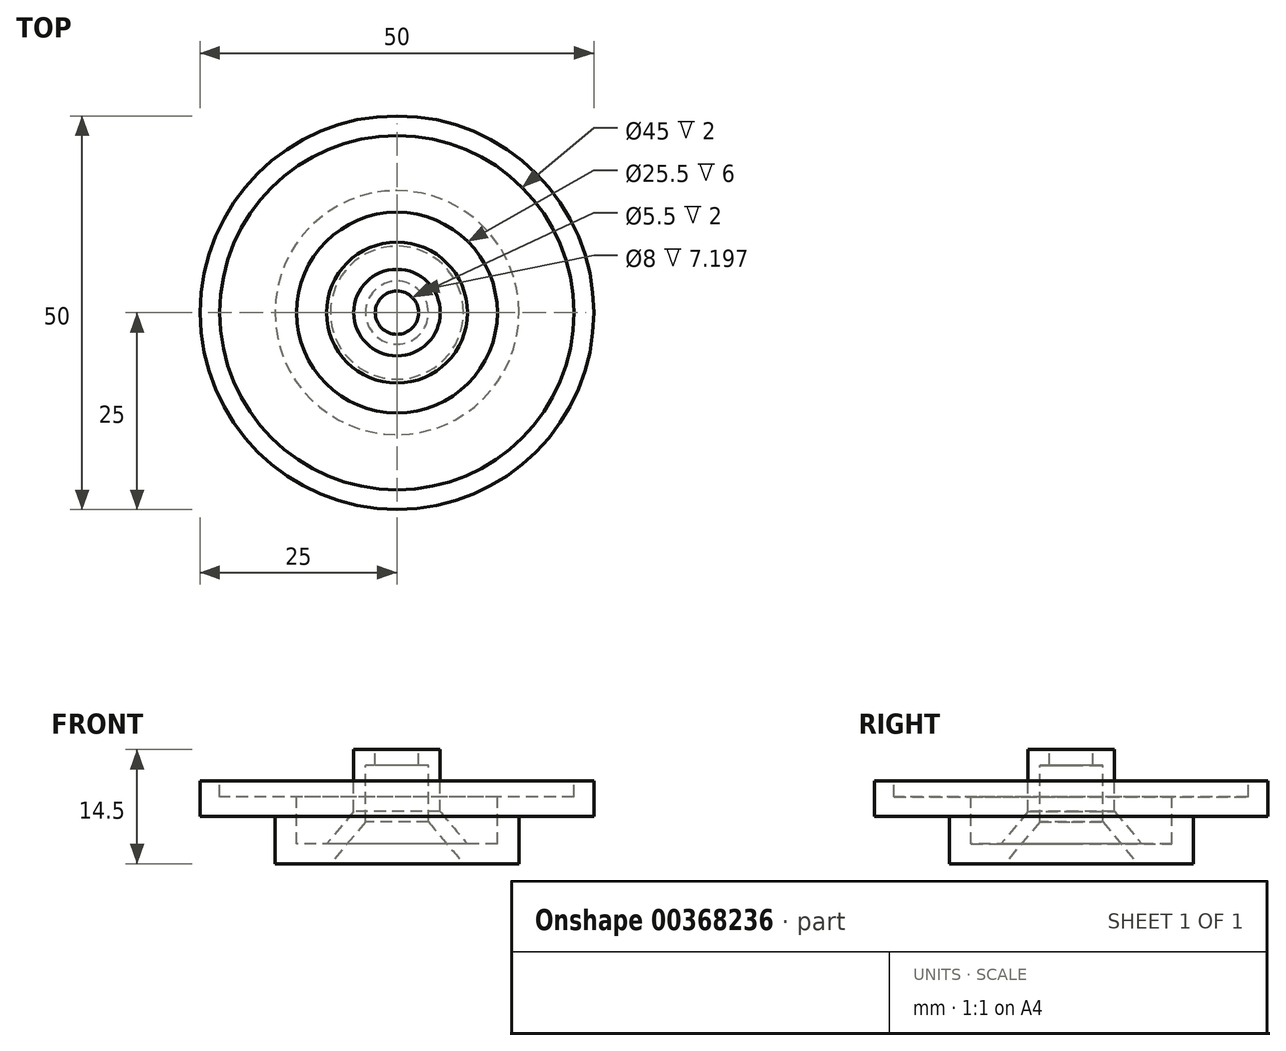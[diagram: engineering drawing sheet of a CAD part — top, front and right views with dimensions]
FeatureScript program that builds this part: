
annotation { "Feature Type Name" : "Feature", "Feature Type Description" : "" }
export const myFeature = defineFeature(function(context is Context, id is Id, definition is map)
    precondition{}
    {
        {
            var Q0;
            Q0=qCreatedBy(makeId("Front.planeOp"),FACE);
            var sketch = newSketch(context, id + "F0", { "sketchPlane" : qUnion([Q0])});
            skLineSegment(sketch, "E0", {"start": v(15.5, 0) * mm, "end": v(15.5, 6) * mm});
            skLineSegment(sketch, "E1", {"start": v(15.5, 6) * mm, "end": v(25, 6) * mm});
            skLineSegment(sketch, "E2", {"start": v(25, 6) * mm, "end": v(25, 10.5) * mm});
            skLineSegment(sketch, "E3", {"start": v(25, 10.5) * mm, "end": v(22.5, 10.5) * mm});
            skLineSegment(sketch, "E4", {"start": v(22.5, 10.5) * mm, "end": v(22.5, 8.5) * mm});
            skLineSegment(sketch, "E5", {"start": v(22.5, 8.5) * mm, "end": v(12.75, 8.5) * mm});
            skLineSegment(sketch, "E6", {"start": v(5.5, 8.5) * mm, "end": v(5.5, 10.5) * mm});
            skLineSegment(sketch, "E7", {"start": v(12.75, 8.5) * mm, "end": v(12.75, 2.5) * mm});
            skLineSegment(sketch, "E8", {"start": v(0, 20.78) * mm, "end": v(0, -15.3) * mm, "construction": true});
            skLineSegment(sketch, "E9", {"start": v(12.75, 2.5) * mm, "end": v(8.95, 2.5) * mm});
            skLineSegment(sketch, "E10", {"start": v(8.95, 2.5) * mm, "end": v(5.5, 6.61) * mm});
            skLineSegment(sketch, "E11", {"start": v(5.5, 8.5) * mm, "end": v(5.5, 6.61) * mm});
            skLineSegment(sketch, "E12", {"start": v(5.5, 10.5) * mm, "end": v(5.5, 14.5) * mm});
            skLineSegment(sketch, "E13", {"start": v(15.5, 0) * mm, "end": v(8.45, 0) * mm});
            skLineSegment(sketch, "E14.trimOffspring", {"start": v(8.45, 0) * mm, "end": v(15.5, 0) * mm});
            skLineSegment(sketch, "E15", {"start": v(4, 12.5) * mm, "end": v(4, 5.3) * mm});
            skLineSegment(sketch, "E16", {"start": v(8.45, 0) * mm, "end": v(4, 5.3) * mm});
            skPoint(sketch, "E17.end.orphan", {"position": v(0, 14.5) * mm});
            skPoint(sketch, "E18.start.orphan", {"position": v(0, 12.5) * mm});
            skLineSegment(sketch, "E19", {"start": v(5.5, 14.5) * mm, "end": v(2.75, 14.5) * mm});
            skLineSegment(sketch, "E20", {"start": v(2.75, 14.5) * mm, "end": v(2.75, 12.5) * mm});
            skLineSegment(sketch, "E21", {"start": v(2.75, 12.5) * mm, "end": v(4, 12.5) * mm});
            skSolve(sketch);
        }
        {
            var Q0;
            Q0=makeQuery(id+"F0.imprint","IMPRINT",FACE,{"disambiguationData":[TD([[makeQuery(id+"F0.imprint","IMPRINT",EDGE,{"derivedFrom":sQuery(id+"F0.wireOp",EDGE,"E0")}),1.0]])]});
            var Q1;
            Q1=sQuery(id+"F0.wireOp",EDGE,"E8");
            revolve(context, id + "F1", {"entities" : qUnion([Q0]), "axis" : qUnion([Q1]), "revolveType" : RevolveType.FULL});
        }
    });
